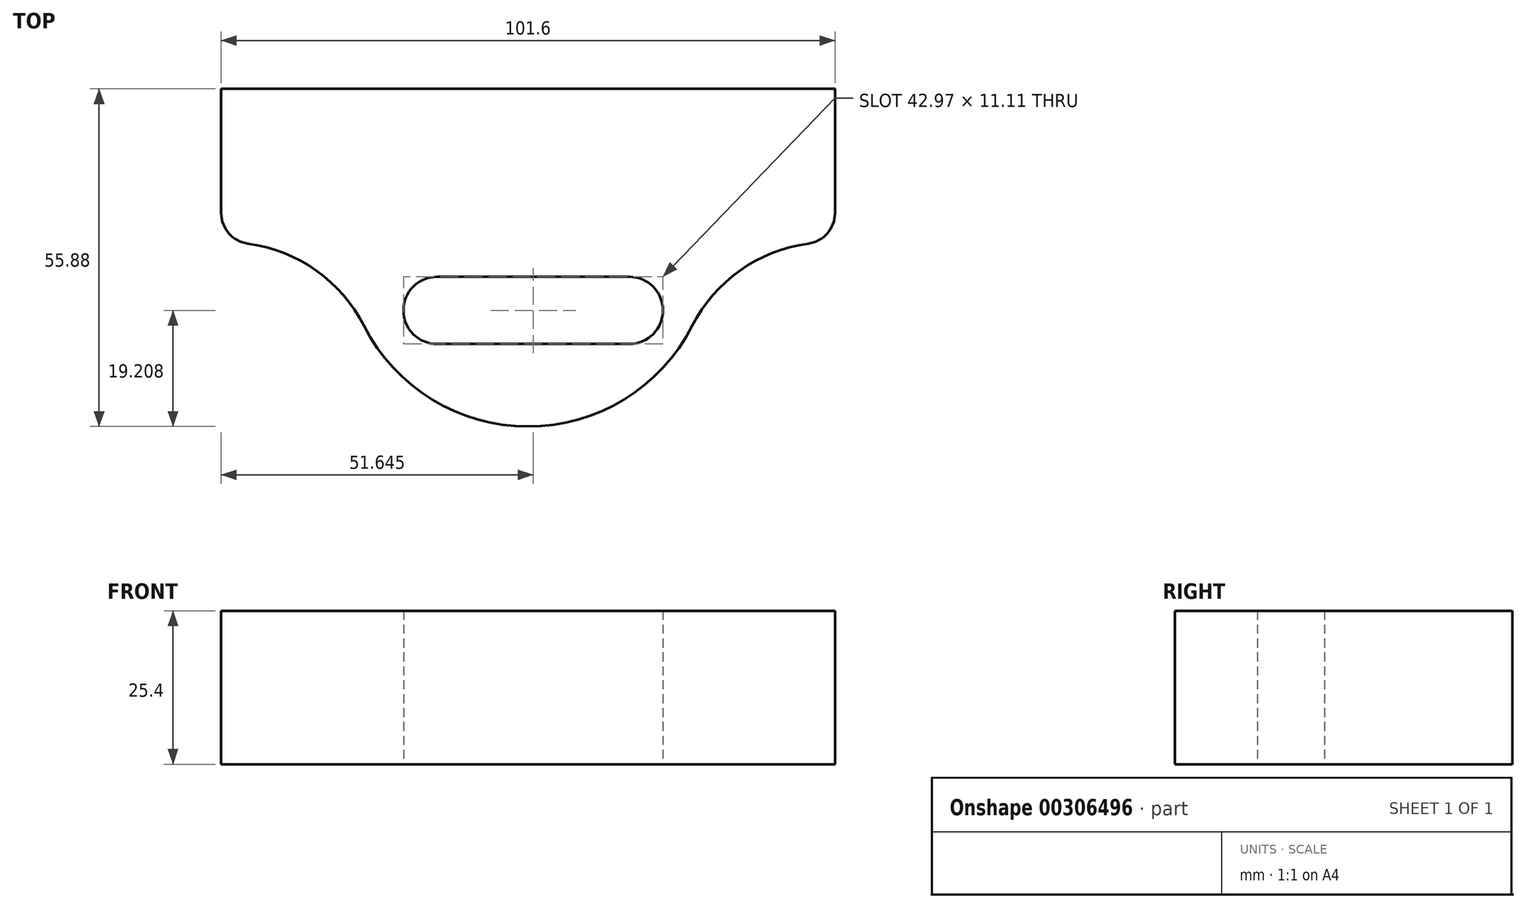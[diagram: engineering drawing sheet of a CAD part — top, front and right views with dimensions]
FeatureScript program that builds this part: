
annotation { "Feature Type Name" : "Feature", "Feature Type Description" : "" }
export const myFeature = defineFeature(function(context is Context, id is Id, definition is map)
    precondition{}
    {
        {
            var Q0;
            Q0=qCreatedBy(makeId("Top.planeOp"),FACE);
            var sketch = newSketch(context, id + "F0", { "sketchPlane" : qUnion([Q0])});
            skLineSegment(sketch, "E0.bottom", {"start": v(-50.8, 25.4) * mm, "end": v(50.8, 25.4) * mm});
            skLineSegment(sketch, "E0.top", {"start": v(-50.8, 0) * mm, "end": v(50.8, 0) * mm});
            skLineSegment(sketch, "E0.left", {"start": v(-50.8, 25.4) * mm, "end": v(-50.8, 0) * mm});
            skLineSegment(sketch, "E0.right", {"start": v(50.8, 25.4) * mm, "end": v(50.8, 0) * mm});
            skArc(sketch, "E1", {"start": v(-27.15, -13.84) * mm, "mid": v(-36.95, -3.46) * mm, "end": v(-50.8, 0) * mm});
            skArc(sketch, "E2", {"start": v(-27.15, -13.84) * mm, "mid": v(0, -30.48) * mm, "end": v(27.15, -13.84) * mm});
            skArc(sketch, "E3", {"start": v(50.8, 0) * mm, "mid": v(36.95, -3.46) * mm, "end": v(27.15, -13.84) * mm});
            skArc(sketch, "E4", {"start": v(-15.08, -5.72) * mm, "mid": v(-20.64, -11.27) * mm, "end": v(-15.08, -16.83) * mm});
            skArc(sketch, "E5", {"start": v(16.77, -16.83) * mm, "mid": v(22.33, -11.27) * mm, "end": v(16.77, -5.72) * mm});
            skLineSegment(sketch, "E6", {"start": v(-15.08, -5.72) * mm, "end": v(16.77, -5.72) * mm});
            skLineSegment(sketch, "E7", {"start": v(-15.08, -16.83) * mm, "end": v(16.77, -16.83) * mm});
            skSolve(sketch);
        }
        {
            var Q0;
            Q0 = qSketchRegion(id + "F0", true);
            extrude(context, id + "F1", {"entities" : qUnion([Q0]), "depth" : 25.4 * mm});
        }
        {
            var Q0;
            Q0=makeQuery(id+"F1.opExtrude","SWEPT_EDGE",EDGE,{"disambiguationData":[OSD([sQuery(id+"F0.wireOp",EDGE,"E0.top"),sQuery(id+"F0.wireOp",EDGE,"E0.left"),sQuery(id+"F0.wireOp",EDGE,"E1")])]});
            var Q1;
            Q1=makeQuery(id+"F1.opExtrude","SWEPT_EDGE",EDGE,{"disambiguationData":[OSD([sQuery(id+"F0.wireOp",EDGE,"E0.top"),sQuery(id+"F0.wireOp",EDGE,"E0.right"),sQuery(id+"F0.wireOp",EDGE,"E3")])]});
            fillet(context, id + "F2", {"entities" : qUnion([Q0, Q1]), "radius" : 5.08 * mm, "tangentPropagation" : true, "allowEdgeOverflow" : false});
        }
    });
